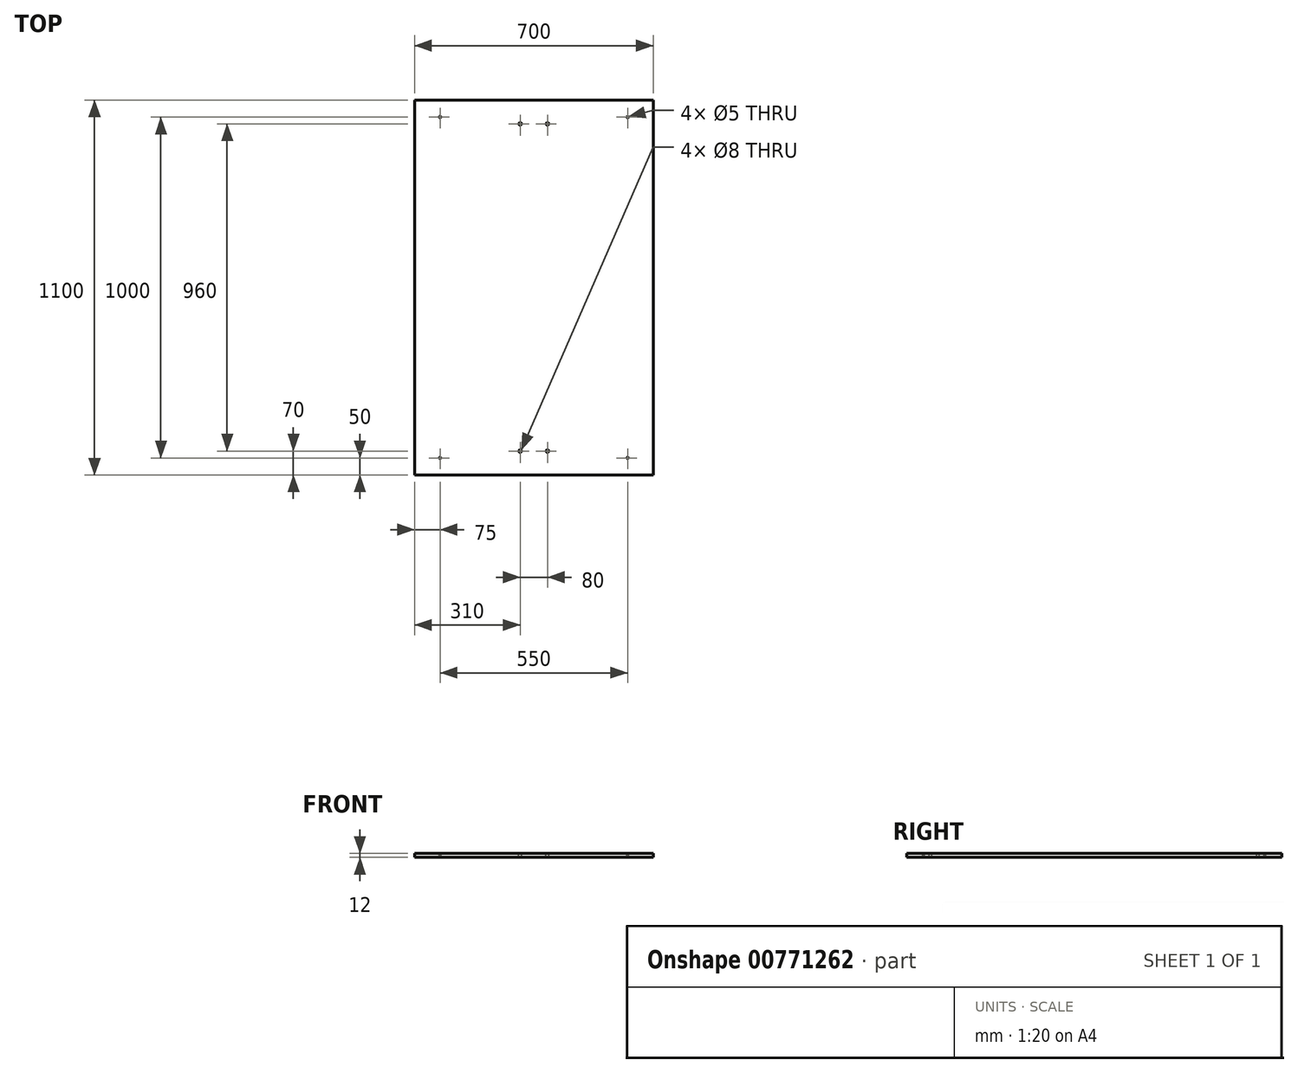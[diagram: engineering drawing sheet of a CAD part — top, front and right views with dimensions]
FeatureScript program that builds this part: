
annotation { "Feature Type Name" : "Feature", "Feature Type Description" : "" }
export const myFeature = defineFeature(function(context is Context, id is Id, definition is map)
    precondition{}
    {
        {
            var Q0;
            Q0=qCreatedBy(makeId("Top.planeOp"),FACE);
            var sketch = newSketch(context, id + "F0", { "sketchPlane" : qUnion([Q0])});
            skLineSegment(sketch, "E0.bottom", {"start": v(350, -550) * mm, "end": v(-350, -550) * mm});
            skLineSegment(sketch, "E0.top", {"start": v(350, 550) * mm, "end": v(-350, 550) * mm});
            skLineSegment(sketch, "E0.left", {"start": v(350, -550) * mm, "end": v(350, 550) * mm});
            skLineSegment(sketch, "E0.right", {"start": v(-350, -550) * mm, "end": v(-350, 550) * mm});
            skPoint(sketch, "E0.middle", {"position": v(0, 0) * mm});
            skSolve(sketch);
        }
        {
            var Q0;
            Q0 = qSketchRegion(id + "F0", true);
            extrude(context, id + "F1", {"entities" : qUnion([Q0]), "depth" : 12 * mm, "offsetDistance" : 25 * mm});
        }
        {
            var Q0;
            Q0=makeQuery(id+"F1.opExtrude","CAP_FACE",FACE,{"disambiguationData":[OSD([sQuery(id+"F0.wireOp",EDGE,"E0.bottom"),sQuery(id+"F0.wireOp",EDGE,"E0.top"),sQuery(id+"F0.wireOp",EDGE,"E0.left"),sQuery(id+"F0.wireOp",EDGE,"E0.right")])],"isStart":false});
            var sketch = newSketch(context, id + "F2", { "sketchPlane" : qUnion([Q0])});
            skLineSegment(sketch, "E1.bottom", {"start": v(275, 500) * mm, "end": v(-275, 500) * mm, "construction": true});
            skLineSegment(sketch, "E1.top", {"start": v(275, -500) * mm, "end": v(-275, -500) * mm, "construction": true});
            skLineSegment(sketch, "E1.left", {"start": v(275, 500) * mm, "end": v(275, -500) * mm, "construction": true});
            skLineSegment(sketch, "E1.right", {"start": v(-275, 500) * mm, "end": v(-275, -500) * mm, "construction": true});
            skCircle(sketch, "E2", {"center": v(-275, -500) * mm, "radius": 2.5 * mm});
            skCircle(sketch, "E3", {"center": v(275, -500) * mm, "radius": 2.5 * mm});
            skCircle(sketch, "E4", {"center": v(-275, 500) * mm, "radius": 2.5 * mm});
            skCircle(sketch, "E5", {"center": v(275, 500) * mm, "radius": 2.5 * mm});
            skLineSegment(sketch, "E6.bottom", {"start": v(40, -480) * mm, "end": v(-40, -480) * mm, "construction": true});
            skLineSegment(sketch, "E6.top", {"start": v(40, 480) * mm, "end": v(-40, 480) * mm, "construction": true});
            skLineSegment(sketch, "E6.left", {"start": v(40, -480) * mm, "end": v(40, 480) * mm, "construction": true});
            skLineSegment(sketch, "E6.right", {"start": v(-40, -480) * mm, "end": v(-40, 480) * mm, "construction": true});
            skPoint(sketch, "E6.middle", {"position": v(0, 0) * mm});
            skSolve(sketch);
        }
        {
            var Q0;
            Q0 = qSketchRegion(id + "F2", true);
            extrude(context, id + "F3", {"entities" : qUnion([Q0]), "operationType" : NewBodyOperationType.REMOVE, "endBound" : BoundingType.THROUGH_ALL, "oppositeDirection" : true, "depth" : 25 * mm, "offsetDistance" : 25 * mm});
        }
        {
            var Q0;
            Q0=sQuery(id+"F2.wireOp",VERTEX,"E6.top.start");
            var Q1;
            Q1=sQuery(id+"F2.wireOp",VERTEX,"E6.top.end");
            var Q2;
            Q2=sQuery(id+"F2.wireOp",VERTEX,"E6.bottom.start");
            var Q3;
            Q3=sQuery(id+"F2.wireOp",VERTEX,"E6.bottom.end");
            var Q4;
            Q4=makeQuery(id+"F1.opExtrude","SWEPT_BODY",BODY,{"disambiguationData":[OSD([sQuery(id+"F0.wireOp",EDGE,"E0.bottom"),sQuery(id+"F0.wireOp",EDGE,"E0.top"),sQuery(id+"F0.wireOp",EDGE,"E0.left"),sQuery(id+"F0.wireOp",EDGE,"E0.right")])]});
            hole(context, id + "F4", {"style" : HoleStyle.SIMPLE, "endStyle" : HoleEndStyle.THROUGH, "holeDiameter" : 8 * mm, "majorDiameter" : 5 * mm, "isTappedThrough" : true, "tappedDepth" : 12 * mm, "tapClearance" : 3, "locations" : qUnion([Q0, Q1, Q2, Q3]), "scope" : qUnion([Q4])});
        }
    });
